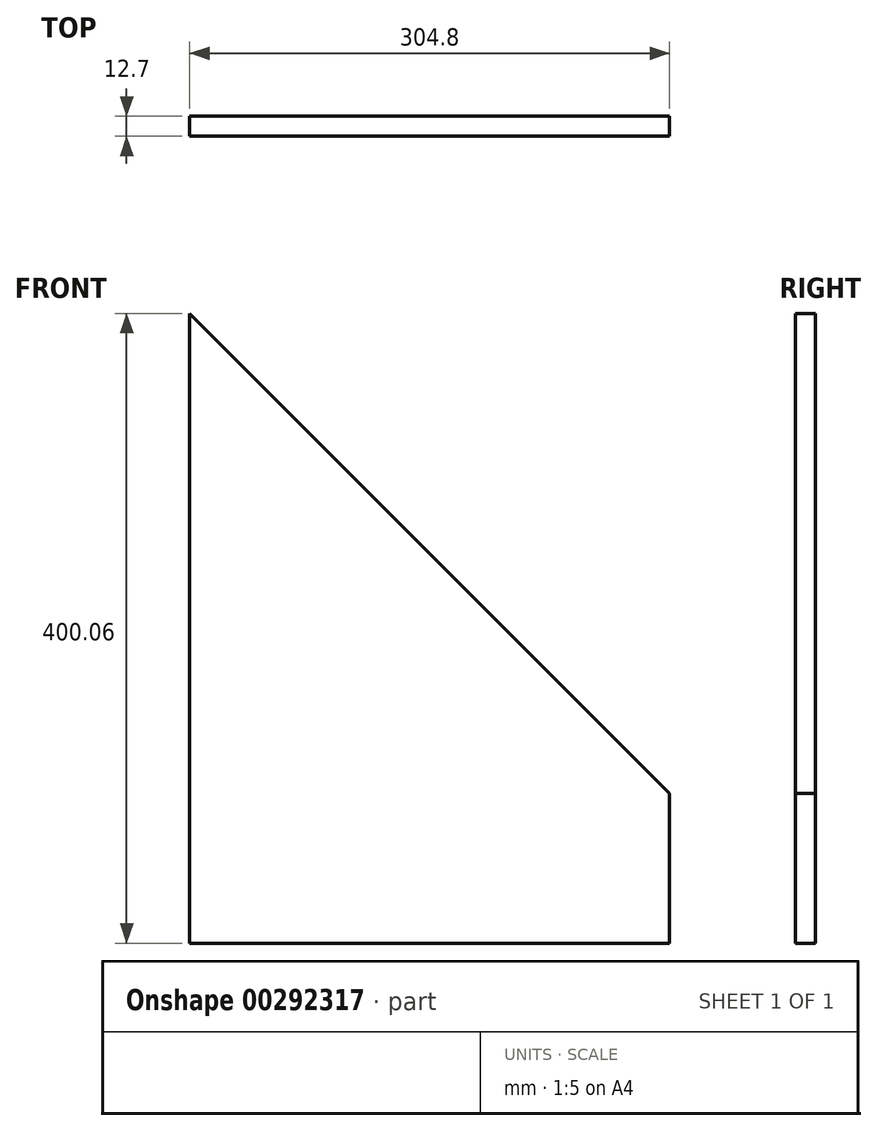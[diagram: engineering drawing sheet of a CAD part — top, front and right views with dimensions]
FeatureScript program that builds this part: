
annotation { "Feature Type Name" : "Feature", "Feature Type Description" : "" }
export const myFeature = defineFeature(function(context is Context, id is Id, definition is map)
    precondition{}
    {
        {
            var Q0;
            Q0=qCreatedBy(makeId("Front.planeOp"),FACE);
            var sketch = newSketch(context, id + "F0", { "sketchPlane" : qUnion([Q0])});
            skLineSegment(sketch, "E0", {"start": v(-152.4, -200.03) * mm, "end": v(152.4, -200.03) * mm});
            skLineSegment(sketch, "E1", {"start": v(152.4, -200.03) * mm, "end": v(152.4, -104.77) * mm});
            skLineSegment(sketch, "E2", {"start": v(152.4, -104.77) * mm, "end": v(-152.4, 200.02) * mm});
            skLineSegment(sketch, "E3", {"start": v(-152.4, 200.02) * mm, "end": v(-152.4, -200.02) * mm});
            skSolve(sketch);
        }
        {
            var Q0;
            Q0=makeQuery(id+"F0.imprint","IMPRINT",FACE,{"disambiguationData":[TD([[makeQuery(id+"F0.imprint","IMPRINT",EDGE,{"derivedFrom":sQuery(id+"F0.wireOp",EDGE,"E0")}),1.0]])]});
            extrude(context, id + "F1", {"entities" : qUnion([Q0]), "depth" : 12.7 * mm});
        }
    });
